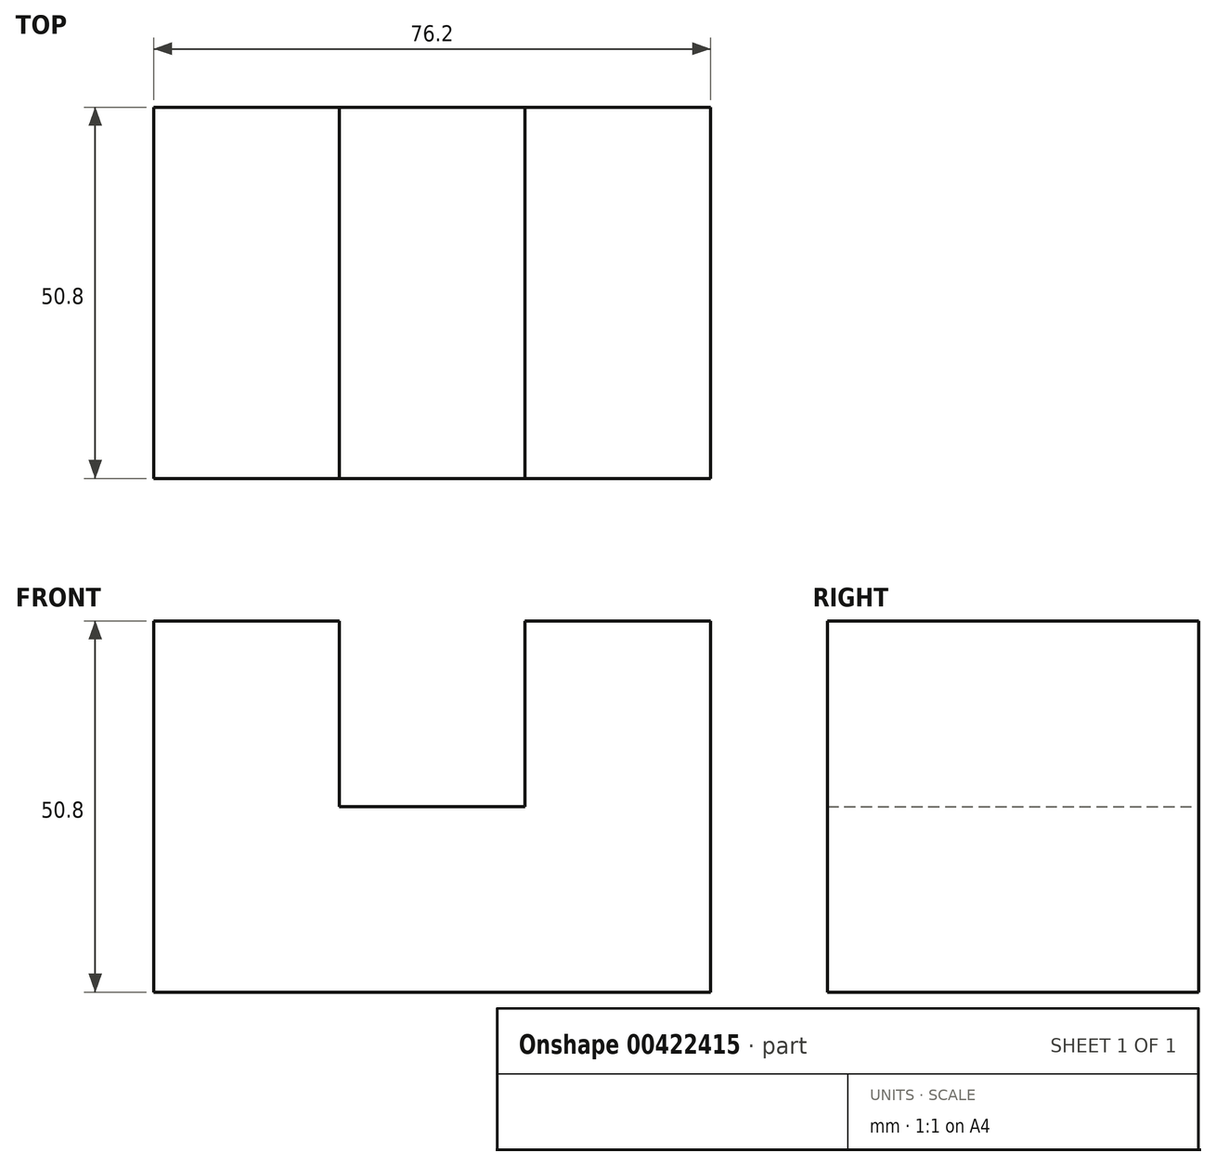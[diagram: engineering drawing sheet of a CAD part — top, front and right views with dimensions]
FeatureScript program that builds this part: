
annotation { "Feature Type Name" : "Feature", "Feature Type Description" : "" }
export const myFeature = defineFeature(function(context is Context, id is Id, definition is map)
    precondition{}
    {
        {
            var Q0;
            Q0=qCreatedBy(makeId("Front.planeOp"),FACE);
            var sketch = newSketch(context, id + "F0", { "sketchPlane" : qUnion([Q0])});
            skLineSegment(sketch, "E0", {"start": v(-46.87, 0) * mm, "end": v(29.33, 0) * mm});
            skLineSegment(sketch, "E1", {"start": v(-46.87, 50.8) * mm, "end": v(-46.87, 0) * mm});
            skLineSegment(sketch, "E2", {"start": v(-46.87, 50.8) * mm, "end": v(-21.47, 50.8) * mm});
            skLineSegment(sketch, "E3", {"start": v(29.33, 0) * mm, "end": v(29.33, 50.8) * mm});
            skLineSegment(sketch, "E4", {"start": v(29.33, 50.8) * mm, "end": v(3.93, 50.8) * mm});
            skLineSegment(sketch, "E5", {"start": v(-21.47, 50.8) * mm, "end": v(-21.47, 25.4) * mm});
            skLineSegment(sketch, "E6", {"start": v(3.93, 50.8) * mm, "end": v(3.93, 25.4) * mm});
            skLineSegment(sketch, "E7", {"start": v(-21.47, 25.4) * mm, "end": v(3.93, 25.4) * mm});
            skSolve(sketch);
        }
        {
            var Q0;
            Q0=makeQuery(id+"F0.imprint","IMPRINT",FACE,{"disambiguationData":[TD([[makeQuery(id+"F0.imprint","IMPRINT",EDGE,{"derivedFrom":sQuery(id+"F0.wireOp",EDGE,"E0")}),1.0]])]});
            extrude(context, id + "F1", {"entities" : qUnion([Q0]), "depth" : 50.8 * mm});
        }
        {
            var Q0;
            Q0 = qSketchRegion(id + "F0", true);
            extrude(context, id + "F2", {"entities" : qUnion([Q0]), "operationType" : NewBodyOperationType.ADD, "depth" : 50.8 * mm});
        }
    });
